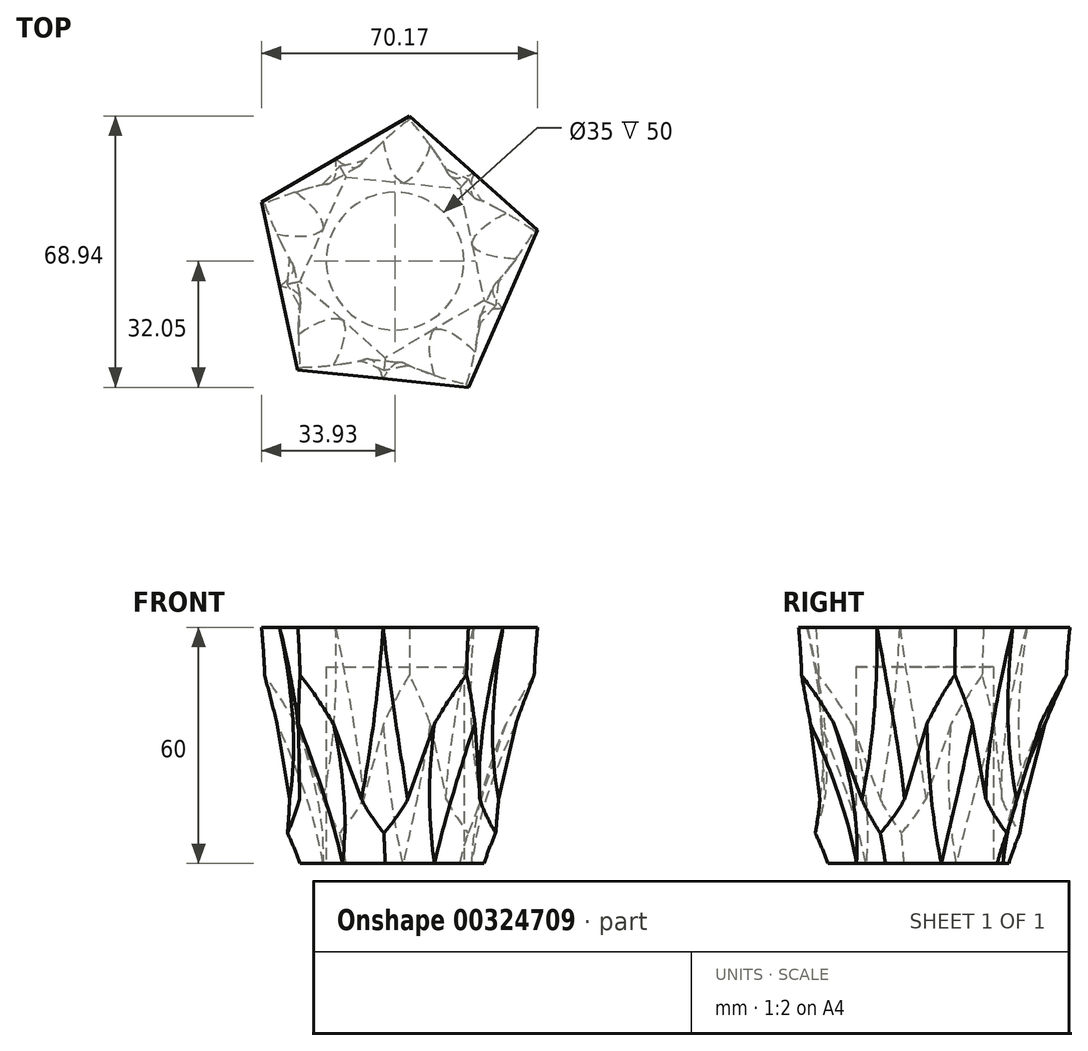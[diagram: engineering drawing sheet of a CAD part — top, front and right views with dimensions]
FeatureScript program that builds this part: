
annotation { "Feature Type Name" : "Feature", "Feature Type Description" : "" }
export const myFeature = defineFeature(function(context is Context, id is Id, definition is map)
    precondition{}
    {
        {
            var Q0;
            Q0=qCreatedBy(makeId("Top.planeOp"),FACE);
            var sketch = newSketch(context, id + "F0", { "sketchPlane" : qUnion([Q0])});
            skCircle(sketch, "E0.cCircle", {"center": v(0, 0) * mm, "radius": 20 * mm, "construction": true});
            skLineSegment(sketch, "E0.0", {"start": v(-12.44, 21.36) * mm, "end": v(16.48, 18.43) * mm});
            skLineSegment(sketch, "E0.1", {"start": v(16.48, 18.43) * mm, "end": v(22.62, -9.97) * mm});
            skLineSegment(sketch, "E0.2", {"start": v(22.62, -9.97) * mm, "end": v(-2.5, -24.6) * mm});
            skLineSegment(sketch, "E0.3", {"start": v(-2.5, -24.6) * mm, "end": v(-24.16, -5.23) * mm});
            skLineSegment(sketch, "E0.4", {"start": v(-24.16, -5.23) * mm, "end": v(-12.44, 21.36) * mm});
            skPoint(sketch, "E0.0.midPoint", {"position": v(2.02, 19.9) * mm});
            skSolve(sketch);
        }
        {
            var Q0;
            Q0=qCreatedBy(makeId("Top.planeOp"),FACE);
            cPlane(context, id + "F1", {"entities" : qUnion([Q0]), "cplaneType" : CPlaneType.OFFSET, "offset" : 60 * mm, "width" : 150 * mm, "height" : 150 * mm});
        }
        {
            var Q0;
            Q0=qCreatedBy(id+"F1.planeOp",FACE);
            var sketch = newSketch(context, id + "F2", { "sketchPlane" : qUnion([Q0])});
            skCircle(sketch, "E1.cCircle", {"center": v(0, 0) * mm, "radius": 30 * mm, "construction": true});
            skLineSegment(sketch, "E1.0", {"start": v(3.74, 36.9) * mm, "end": v(36.24, 7.84) * mm});
            skLineSegment(sketch, "E1.1", {"start": v(36.24, 7.84) * mm, "end": v(18.66, -32.05) * mm});
            skLineSegment(sketch, "E1.2", {"start": v(18.66, -32.05) * mm, "end": v(-24.71, -27.65) * mm});
            skLineSegment(sketch, "E1.3", {"start": v(-24.71, -27.65) * mm, "end": v(-33.93, 14.96) * mm});
            skLineSegment(sketch, "E1.4", {"start": v(-33.93, 14.96) * mm, "end": v(3.74, 36.9) * mm});
            skPoint(sketch, "E1.0.midPoint", {"position": v(20, 22.37) * mm});
            skSolve(sketch);
        }
        {
            var Q0;
            Q0 = qSketchRegion(id + "F2", true);
            var Q1;
            Q1 = qSketchRegion(id + "F0", true);
            loft(context, id + "F3", {"sheetProfilesArray" : [{ "sheetProfileEntities" : qUnion([Q0]) }, { "sheetProfileEntities" : qUnion([Q1]) }]});
        }
        {
            var Q0;
            Q0=makeQuery(id+"F3.opLoft","MID_CAP_VERTEX",VERTEX,{"disambiguationData":[OSD([sQuery(id+"F2.wireOp",EDGE,"E1.1"),sQuery(id+"F2.wireOp",EDGE,"E1.2")])],"capPos":0.0});
            var Q1;
            Q1=makeQuery(id+"F3.opLoft","MID_CAP_VERTEX",VERTEX,{"disambiguationData":[OSD([sQuery(id+"F0.wireOp",EDGE,"E0.1"),sQuery(id+"F0.wireOp",EDGE,"E0.2")])],"capPos":1.0});
            var Q2;
            Q2=makeQuery(id+"F3.opLoft","MID_CAP_VERTEX",VERTEX,{"disambiguationData":[OSD([sQuery(id+"F2.wireOp",EDGE,"E1.3"),sQuery(id+"F2.wireOp",EDGE,"E1.4")])],"capPos":0.0});
            cPlane(context, id + "F4", {"entities" : qUnion([Q0, Q1, Q2]), "cplaneType" : CPlaneType.THREE_POINT, "offset" : 25 * mm, "width" : 150 * mm, "height" : 150 * mm});
        }
        {
            var Q0;
            Q0=qCreatedBy(id+"F4.planeOp",FACE);
            var sketch = newSketch(context, id + "F5", { "sketchPlane" : qUnion([Q0])});
            skLineSegment(sketch, "E2", {"start": v(23.3, 3.92) * mm, "end": v(18.17, 67.76) * mm});
            skSolve(sketch);
        }
        {
            var Q1;
            Q1 = qSketchRegion(id + "F2", true);
            var Q2;
            Q2 = qSketchRegion(id + "F0", true);
            var Q3;
            Q3=sQuery(id+"F5.wireOp",EDGE,"E2");
            loft(context, id + "F6", {"operationType" : NewBodyOperationType.ADD, "addGuides" : true, "sheetProfilesArray" : [{ "sheetProfileEntities" : qUnion([Q1]) }, { "sheetProfileEntities" : qUnion([Q2]) }], "guidesArray" : [{ "guideEntities" : qUnion([Q3]), "guideDerivativeType" : LoftGuideDerivativeType.DEFAULT, "guideDerivativeMagnitude" : 1 }]});
        }
        {
            var Q0;
            Q0=makeQuery(id+"F3.opLoft","CAP_FACE",FACE,{"disambiguationData":[OSD([makeQuery(id+"F0.imprint","IMPRINT",FACE,{"disambiguationData":[TD([[makeQuery(id+"F0.imprint","IMPRINT",EDGE,{"derivedFrom":sQuery(id+"F0.wireOp",EDGE,"E0.0")}),-1.0]])]})])],"isStart":true});
            var sketch = newSketch(context, id + "F7", { "sketchPlane" : qUnion([Q0])});
            skCircle(sketch, "E3", {"center": v(0, 0) * mm, "radius": 17.5 * mm});
            skSolve(sketch);
        }
        {
            var Q0;
            Q0=makeQuery(id+"F7.imprint","IMPRINT",FACE,{"disambiguationData":[TD([[makeQuery(id+"F7.imprint","IMPRINT",EDGE,{"derivedFrom":sQuery(id+"F7.wireOp",EDGE,"E3")}),1.0]])]});
            extrude(context, id + "F8", {"entities" : qUnion([Q0]), "operationType" : NewBodyOperationType.REMOVE, "oppositeDirection" : true, "depth" : 50 * mm});
        }
        {
            var Q0;
            {var subQ0=sQuery(id+"F2.wireOp",EDGE,"E1.4");var subQ1=sQuery(id+"F2.wireOp",EDGE,"E1.3");var subQ2=sQuery(id+"F0.wireOp",EDGE,"E0.4");var subQ3=sQuery(id+"F0.wireOp",EDGE,"E0.3");var subQ4=sQuery(id+"F0.wireOp",EDGE,"E0.0");Q0=makeQuery(id+"F6.boolean.opBoolean","INTERSECT",EDGE,{"derivedFrom":[makeQuery(id+"F3.opLoft","SWEPT_FACE",FACE,{"disambiguationData":[OSD([subQ4,subQ3,subQ2,sQuery(id+"F2.wireOp",EDGE,"E1.2"),subQ1,subQ0])]}),makeQuery(id+"F6.opLoft","SWEPT_FACE",FACE,{"disambiguationData":[OSD([subQ4,subQ3,subQ2,sQuery(id+"F2.wireOp",EDGE,"E1.0"),subQ1,subQ0])]})]});}
            var Q1;
            {var subQ0=sQuery(id+"F2.wireOp",EDGE,"E1.4");var subQ1=sQuery(id+"F2.wireOp",EDGE,"E1.3");var subQ2=sQuery(id+"F2.wireOp",EDGE,"E1.0");var subQ3=sQuery(id+"F0.wireOp",EDGE,"E0.4");var subQ4=sQuery(id+"F0.wireOp",EDGE,"E0.0");Q1=makeQuery(id+"F6.boolean.opBoolean","INTERSECT",EDGE,{"derivedFrom":[makeQuery(id+"F3.opLoft","SWEPT_FACE",FACE,{"disambiguationData":[OSD([subQ4,sQuery(id+"F0.wireOp",EDGE,"E0.1"),subQ3,subQ2,subQ1,subQ0])]}),makeQuery(id+"F6.opLoft","SWEPT_FACE",FACE,{"disambiguationData":[OSD([subQ4,sQuery(id+"F0.wireOp",EDGE,"E0.3"),subQ3,subQ2,subQ1,subQ0])]})]});}
            var Q2;
            {var subQ0=sQuery(id+"F2.wireOp",EDGE,"E1.4");var subQ1=sQuery(id+"F2.wireOp",EDGE,"E1.0");var subQ2=sQuery(id+"F0.wireOp",EDGE,"E0.4");var subQ3=sQuery(id+"F0.wireOp",EDGE,"E0.1");var subQ4=sQuery(id+"F0.wireOp",EDGE,"E0.0");Q2=makeQuery(id+"F6.boolean.opBoolean","INTERSECT",EDGE,{"derivedFrom":[makeQuery(id+"F3.opLoft","SWEPT_FACE",FACE,{"disambiguationData":[OSD([subQ4,subQ3,subQ2,subQ1,sQuery(id+"F2.wireOp",EDGE,"E1.3"),subQ0])]}),makeQuery(id+"F6.opLoft","SWEPT_FACE",FACE,{"disambiguationData":[OSD([subQ4,subQ3,subQ2,subQ1,sQuery(id+"F2.wireOp",EDGE,"E1.1"),subQ0])]})]});}
            var Q3;
            {var subQ0=sQuery(id+"F2.wireOp",EDGE,"E1.4");var subQ1=sQuery(id+"F2.wireOp",EDGE,"E1.1");var subQ2=sQuery(id+"F2.wireOp",EDGE,"E1.0");var subQ3=sQuery(id+"F0.wireOp",EDGE,"E0.1");var subQ4=sQuery(id+"F0.wireOp",EDGE,"E0.0");Q3=makeQuery(id+"F6.boolean.opBoolean","INTERSECT",EDGE,{"derivedFrom":[makeQuery(id+"F3.opLoft","SWEPT_FACE",FACE,{"disambiguationData":[OSD([subQ4,subQ3,sQuery(id+"F0.wireOp",EDGE,"E0.2"),subQ2,subQ1,subQ0])]}),makeQuery(id+"F6.opLoft","SWEPT_FACE",FACE,{"disambiguationData":[OSD([subQ4,subQ3,sQuery(id+"F0.wireOp",EDGE,"E0.4"),subQ2,subQ1,subQ0])]})]});}
            var Q4;
            {var subQ0=sQuery(id+"F2.wireOp",EDGE,"E1.1");var subQ1=sQuery(id+"F2.wireOp",EDGE,"E1.0");var subQ2=sQuery(id+"F0.wireOp",EDGE,"E0.1");var subQ3=sQuery(id+"F0.wireOp",EDGE,"E0.0");Q4=makeQuery(id+"F6.boolean.opBoolean","INTERSECT",EDGE,{"derivedFrom":[makeQuery(id+"F3.opLoft","SWEPT_FACE",FACE,{"disambiguationData":[OSD([subQ3,subQ2,sQuery(id+"F0.wireOp",EDGE,"E0.2"),subQ1,subQ0,sQuery(id+"F2.wireOp",EDGE,"E1.4")])]}),makeQuery(id+"F6.opLoft","SWEPT_FACE",FACE,{"disambiguationData":[OSD([subQ3,subQ2,subQ1,subQ0,sQuery(id+"F5.wireOp",EDGE,"E2")])]})]});}
            var Q5;
            {var subQ0=sQuery(id+"F2.wireOp",EDGE,"E1.1");var subQ1=sQuery(id+"F2.wireOp",EDGE,"E1.0");var subQ2=sQuery(id+"F0.wireOp",EDGE,"E0.1");Q5=makeQuery(id+"F6.boolean.opBoolean","INTERSECT",EDGE,{"derivedFrom":[makeQuery(id+"F3.opLoft","SWEPT_FACE",FACE,{"disambiguationData":[OSD([subQ2,sQuery(id+"F0.wireOp",EDGE,"E0.2"),sQuery(id+"F0.wireOp",EDGE,"E0.3"),subQ1,subQ0,sQuery(id+"F2.wireOp",EDGE,"E1.2")])]}),makeQuery(id+"F6.opLoft","SWEPT_FACE",FACE,{"disambiguationData":[OSD([sQuery(id+"F0.wireOp",EDGE,"E0.0"),subQ2,subQ1,subQ0,sQuery(id+"F5.wireOp",EDGE,"E2")])]})]});}
            var Q6;
            {var subQ0=sQuery(id+"F2.wireOp",EDGE,"E1.2");var subQ1=sQuery(id+"F2.wireOp",EDGE,"E1.1");var subQ2=sQuery(id+"F0.wireOp",EDGE,"E0.3");var subQ3=sQuery(id+"F0.wireOp",EDGE,"E0.2");var subQ4=sQuery(id+"F0.wireOp",EDGE,"E0.1");Q6=makeQuery(id+"F6.boolean.opBoolean","INTERSECT",EDGE,{"derivedFrom":[makeQuery(id+"F3.opLoft","SWEPT_FACE",FACE,{"disambiguationData":[OSD([subQ4,subQ3,subQ2,sQuery(id+"F2.wireOp",EDGE,"E1.0"),subQ1,subQ0])]}),makeQuery(id+"F6.opLoft","SWEPT_FACE",FACE,{"disambiguationData":[OSD([subQ4,subQ3,subQ2,subQ1,subQ0,sQuery(id+"F2.wireOp",EDGE,"E1.3"),sQuery(id+"F5.wireOp",EDGE,"E2")])]})]});}
            var Q7;
            {var subQ0=sQuery(id+"F2.wireOp",EDGE,"E1.3");var subQ1=sQuery(id+"F2.wireOp",EDGE,"E1.2");var subQ2=sQuery(id+"F2.wireOp",EDGE,"E1.1");var subQ3=sQuery(id+"F0.wireOp",EDGE,"E0.3");var subQ4=sQuery(id+"F0.wireOp",EDGE,"E0.2");Q7=makeQuery(id+"F6.boolean.opBoolean","INTERSECT",EDGE,{"derivedFrom":[makeQuery(id+"F3.opLoft","SWEPT_FACE",FACE,{"disambiguationData":[OSD([subQ4,subQ3,sQuery(id+"F0.wireOp",EDGE,"E0.4"),subQ2,subQ1,subQ0])]}),makeQuery(id+"F6.opLoft","SWEPT_FACE",FACE,{"disambiguationData":[OSD([sQuery(id+"F0.wireOp",EDGE,"E0.1"),subQ4,subQ3,subQ2,subQ1,subQ0,sQuery(id+"F5.wireOp",EDGE,"E2")])]})]});}
            var Q8;
            {var subQ0=sQuery(id+"F2.wireOp",EDGE,"E1.3");var subQ1=sQuery(id+"F2.wireOp",EDGE,"E1.2");var subQ2=sQuery(id+"F0.wireOp",EDGE,"E0.4");var subQ3=sQuery(id+"F0.wireOp",EDGE,"E0.3");var subQ4=sQuery(id+"F0.wireOp",EDGE,"E0.2");Q8=makeQuery(id+"F6.boolean.opBoolean","INTERSECT",EDGE,{"derivedFrom":[makeQuery(id+"F3.opLoft","SWEPT_FACE",FACE,{"disambiguationData":[OSD([subQ4,subQ3,subQ2,sQuery(id+"F2.wireOp",EDGE,"E1.1"),subQ1,subQ0])]}),makeQuery(id+"F6.opLoft","SWEPT_FACE",FACE,{"disambiguationData":[OSD([subQ4,subQ3,subQ2,subQ1,subQ0,sQuery(id+"F2.wireOp",EDGE,"E1.4")])]})]});}
            var Q9;
            {var subQ0=sQuery(id+"F2.wireOp",EDGE,"E1.4");var subQ1=sQuery(id+"F2.wireOp",EDGE,"E1.3");var subQ2=sQuery(id+"F2.wireOp",EDGE,"E1.2");var subQ3=sQuery(id+"F0.wireOp",EDGE,"E0.4");var subQ4=sQuery(id+"F0.wireOp",EDGE,"E0.3");Q9=makeQuery(id+"F6.boolean.opBoolean","INTERSECT",EDGE,{"derivedFrom":[makeQuery(id+"F3.opLoft","SWEPT_FACE",FACE,{"disambiguationData":[OSD([sQuery(id+"F0.wireOp",EDGE,"E0.0"),subQ4,subQ3,subQ2,subQ1,subQ0])]}),makeQuery(id+"F6.opLoft","SWEPT_FACE",FACE,{"disambiguationData":[OSD([sQuery(id+"F0.wireOp",EDGE,"E0.2"),subQ4,subQ3,subQ2,subQ1,subQ0])]})]});}
            chamfer(context, id + "F9", {"entities" : qUnion([Q0, Q1, Q2, Q3, Q4, Q5, Q6, Q7, Q8, Q9]), "width" : 15 * mm, "tangentPropagation" : true});
        }
    });
